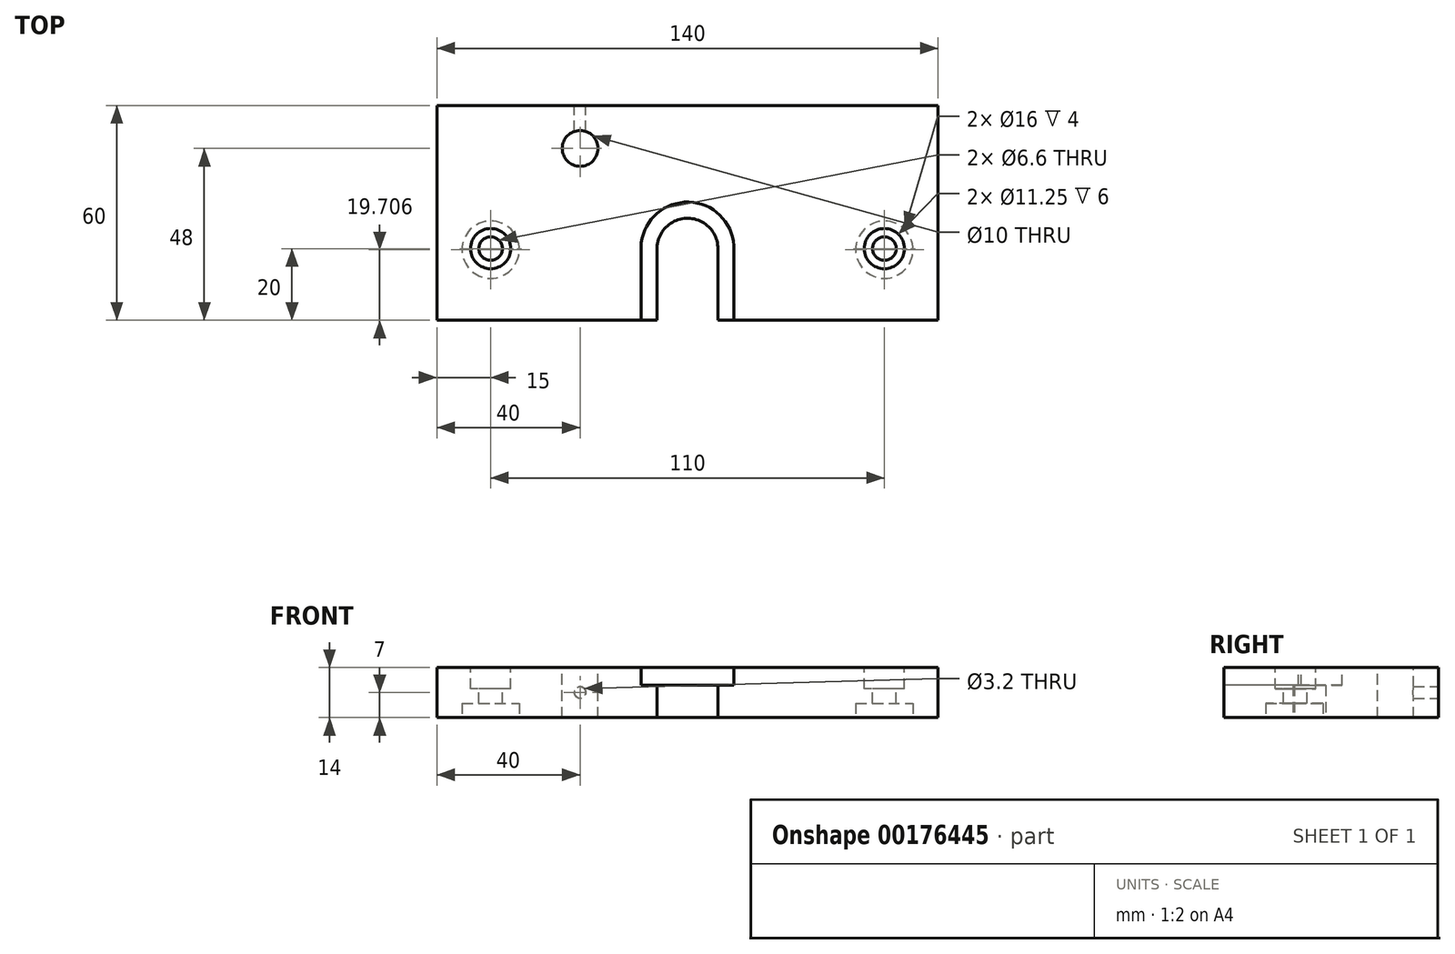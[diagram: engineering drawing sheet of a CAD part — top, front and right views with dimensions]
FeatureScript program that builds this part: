
annotation { "Feature Type Name" : "Feature", "Feature Type Description" : "" }
export const myFeature = defineFeature(function(context is Context, id is Id, definition is map)
    precondition{}
    {
        {
            var Q0;
            Q0=qCreatedBy(makeId("Top.planeOp"),FACE);
            var sketch = newSketch(context, id + "F0", { "sketchPlane" : qUnion([Q0])});
            skLineSegment(sketch, "E0.bottom", {"start": v(70, -30) * mm, "end": v(8.47, -30) * mm});
            skLineSegment(sketch, "E0.top", {"start": v(70, 30) * mm, "end": v(-70, 30) * mm});
            skLineSegment(sketch, "E0.left", {"start": v(70, -30) * mm, "end": v(70, 30) * mm});
            skLineSegment(sketch, "E0.right", {"start": v(-70, -30) * mm, "end": v(-70, 30) * mm});
            skPoint(sketch, "E0.middle", {"position": v(0, 0) * mm});
            skLineSegment(sketch, "E1.trimOffspring", {"start": v(-8.5, -30) * mm, "end": v(-70, -30) * mm});
            skPoint(sketch, "E2.center.orphan", {"position": v(0, -10) * mm});
            skArc(sketch, "E3", {"start": v(8.47, -10.67) * mm, "mid": v(0.19, -1.5) * mm, "end": v(-8.5, -10.3) * mm});
            skLineSegment(sketch, "E4", {"start": v(-8.5, -9.7) * mm, "end": v(-8.5, -30) * mm});
            skLineSegment(sketch, "E5", {"start": v(8.47, -10.67) * mm, "end": v(8.47, -30) * mm});
            skSolve(sketch);
        }
        {
            var Q0;
            Q0=makeQuery(id+"F0.imprint","IMPRINT",FACE,{"disambiguationData":[TD([[makeQuery(id+"F0.imprint","IMPRINT",EDGE,{"derivedFrom":sQuery(id+"F0.wireOp",EDGE,"E0.bottom")}),-1.0]])]});
            extrude(context, id + "F1", {"entities" : qUnion([Q0]), "depth" : 14 * mm});
        }
        {
            var Q0;
            Q0=makeQuery(id+"F1.opExtrude","CAP_FACE",FACE,{"disambiguationData":[OSD([sQuery(id+"F0.wireOp",EDGE,"E0.bottom"),sQuery(id+"F0.wireOp",EDGE,"E0.top"),sQuery(id+"F0.wireOp",EDGE,"E0.left"),sQuery(id+"F0.wireOp",EDGE,"E0.right"),sQuery(id+"F0.wireOp",EDGE,"E1.trimOffspring"),sQuery(id+"F0.wireOp",EDGE,"E3"),sQuery(id+"F0.wireOp",EDGE,"E4"),sQuery(id+"F0.wireOp",EDGE,"E5")])],"isStart":false});
            var sketch = newSketch(context, id + "F2", { "sketchPlane" : qUnion([Q0])});
            skArc(sketch, "E6", {"start": v(12.97, -10.87) * mm, "mid": v(-0.37, 3) * mm, "end": v(-12.9, -11.6) * mm});
            skLineSegment(sketch, "E7", {"start": v(-12.9, -8.4) * mm, "end": v(-12.9, -30) * mm});
            skLineSegment(sketch, "E8", {"start": v(12.97, -9.13) * mm, "end": v(12.97, -30) * mm});
            skSolve(sketch);
        }
        {
            var Q0;
            Q0=makeQuery(id+"F2.imprint","IMPRINT",FACE,{"disambiguationData":[TD([[makeQuery(id+"F2.imprint","IMPRINT",EDGE,{"derivedFrom":makeQuery(id+"F1.opExtrude","CAP_EDGE",EDGE,{"disambiguationData":[OSD([sQuery(id+"F0.wireOp",EDGE,"E3")])],"isStart":false})}),-1.0]])]});
            extrude(context, id + "F3", {"entities" : qUnion([Q0]), "operationType" : NewBodyOperationType.REMOVE, "oppositeDirection" : true, "depth" : 5 * mm});
        }
        {
            var Q0;
            Q0=makeQuery(id+"F1.opExtrude","CAP_FACE",FACE,{"disambiguationData":[OSD([sQuery(id+"F0.wireOp",EDGE,"E0.bottom"),sQuery(id+"F0.wireOp",EDGE,"E0.top"),sQuery(id+"F0.wireOp",EDGE,"E0.left"),sQuery(id+"F0.wireOp",EDGE,"E0.right"),sQuery(id+"F0.wireOp",EDGE,"E1.trimOffspring"),sQuery(id+"F0.wireOp",EDGE,"E3"),sQuery(id+"F0.wireOp",EDGE,"E4"),sQuery(id+"F0.wireOp",EDGE,"E5")])],"isStart":false});
            var sketch = newSketch(context, id + "F4", { "sketchPlane" : qUnion([Q0])});
            skCircle(sketch, "E9", {"center": v(-30, 18) * mm, "radius": 5 * mm});
            skSolve(sketch);
        }
        {
            var Q0;
            Q0=sQuery(id+"F4.wireOp",VERTEX,"E9.center");
            var Q1;
            Q1=makeQuery(id+"F1.opExtrude","SWEPT_BODY",BODY,{"disambiguationData":[OSD([sQuery(id+"F0.wireOp",EDGE,"E0.bottom"),sQuery(id+"F0.wireOp",EDGE,"E0.top"),sQuery(id+"F0.wireOp",EDGE,"E0.left"),sQuery(id+"F0.wireOp",EDGE,"E0.right"),sQuery(id+"F0.wireOp",EDGE,"E1.trimOffspring"),sQuery(id+"F0.wireOp",EDGE,"E3"),sQuery(id+"F0.wireOp",EDGE,"E4"),sQuery(id+"F0.wireOp",EDGE,"E5")])]});
            hole(context, id + "F5", {"style" : HoleStyle.SIMPLE, "endStyle" : HoleEndStyle.THROUGH, "holeDiameter" : 10 * mm, "startFromSketch" : true, "locations" : qUnion([Q0]), "scope" : qUnion([Q1]), "isTappedThrough" : true});
        }
        {
            var Q0;
            Q0=makeQuery(id+"F1.opExtrude","CAP_FACE",FACE,{"disambiguationData":[OSD([sQuery(id+"F0.wireOp",EDGE,"E0.bottom"),sQuery(id+"F0.wireOp",EDGE,"E0.top"),sQuery(id+"F0.wireOp",EDGE,"E0.left"),sQuery(id+"F0.wireOp",EDGE,"E0.right"),sQuery(id+"F0.wireOp",EDGE,"E1.trimOffspring"),sQuery(id+"F0.wireOp",EDGE,"E3"),sQuery(id+"F0.wireOp",EDGE,"E4"),sQuery(id+"F0.wireOp",EDGE,"E5")])],"isStart":true});
            var sketch = newSketch(context, id + "F6", { "sketchPlane" : qUnion([Q0])});
            skCircle(sketch, "E10", {"center": v(-55, 10.3) * mm, "radius": 8 * mm});
            skCircle(sketch, "E11", {"center": v(55, 10.3) * mm, "radius": 8 * mm});
            skSolve(sketch);
        }
        {
            var Q0;
            Q0=makeQuery(id+"F6.imprint","IMPRINT",FACE,{"disambiguationData":[TD([[makeQuery(id+"F6.imprint","IMPRINT",EDGE,{"derivedFrom":sQuery(id+"F6.wireOp",EDGE,"E10")}),1.0]])]});
            var Q1;
            Q1=makeQuery(id+"F6.imprint","IMPRINT",FACE,{"disambiguationData":[TD([[makeQuery(id+"F6.imprint","IMPRINT",EDGE,{"derivedFrom":sQuery(id+"F6.wireOp",EDGE,"E11")}),1.0]])]});
            extrude(context, id + "F7", {"entities" : qUnion([Q0, Q1]), "operationType" : NewBodyOperationType.REMOVE, "oppositeDirection" : true, "depth" : 4 * mm});
        }
        {
            var Q0;
            Q0=makeQuery(id+"F1.opExtrude","CAP_FACE",FACE,{"disambiguationData":[OSD([sQuery(id+"F0.wireOp",EDGE,"E0.bottom"),sQuery(id+"F0.wireOp",EDGE,"E0.top"),sQuery(id+"F0.wireOp",EDGE,"E0.left"),sQuery(id+"F0.wireOp",EDGE,"E0.right"),sQuery(id+"F0.wireOp",EDGE,"E1.trimOffspring"),sQuery(id+"F0.wireOp",EDGE,"E3"),sQuery(id+"F0.wireOp",EDGE,"E4"),sQuery(id+"F0.wireOp",EDGE,"E5")])],"isStart":false});
            var sketch = newSketch(context, id + "F8", { "sketchPlane" : qUnion([Q0])});
            skCircle(sketch, "E12", {"center": v(-55, -10) * mm, "radius": 5 * mm});
            skCircle(sketch, "E13", {"center": v(55, -10) * mm, "radius": 5 * mm});
            skSolve(sketch);
        }
        {
            var Q0;
            Q0=sQuery(id+"F8.wireOp",VERTEX,"E12.center");
            var Q1;
            Q1=sQuery(id+"F8.wireOp",VERTEX,"E13.center");
            var Q2;
            Q2=makeQuery(id+"F1.opExtrude","SWEPT_BODY",BODY,{"disambiguationData":[OSD([sQuery(id+"F0.wireOp",EDGE,"E0.bottom"),sQuery(id+"F0.wireOp",EDGE,"E0.top"),sQuery(id+"F0.wireOp",EDGE,"E0.left"),sQuery(id+"F0.wireOp",EDGE,"E0.right"),sQuery(id+"F0.wireOp",EDGE,"E1.trimOffspring"),sQuery(id+"F0.wireOp",EDGE,"E3"),sQuery(id+"F0.wireOp",EDGE,"E4"),sQuery(id+"F0.wireOp",EDGE,"E5")])]});
            hole(context, id + "F9", {"style" : HoleStyle.C_BORE, "endStyle" : HoleEndStyle.THROUGH, "standardTappedOrClearance" : lookupTablePath({ "standard" : "ISO", "fit" : "Normal", "size" : "M6", "type" : "Clearance" }), "standardBlindInLast" : lookupTablePath({ "fit" : "Standard", "standard" : "ISO", "size" : "M6", "type" : "Clearance" }), "holeDiameter" : 6.6 * mm, "cBoreDiameter" : 11.25 * mm, "cBoreDepth" : 6 * mm, "startFromSketch" : true, "locations" : qUnion([Q0, Q1]), "scope" : qUnion([Q2]), "isTappedThrough" : true});
        }
        {
            var Q0;
            Q0=makeQuery(id+"F1.opExtrude","SWEPT_FACE",FACE,{"disambiguationData":[OSD([sQuery(id+"F0.wireOp",EDGE,"E0.top")])]});
            var sketch = newSketch(context, id + "F10", { "sketchPlane" : qUnion([Q0])});
            skCircle(sketch, "E14", {"center": v(30, 7) * mm, "radius": 2.16 * mm});
            skPoint(sketch, "E14.centerSnap0", {"position": v(70, 7) * mm});
            skSolve(sketch);
        }
        {
            var Q0;
            Q0=sQuery(id+"F10.wireOp",VERTEX,"E14.center");
            var Q1;
            Q1=makeQuery(id+"F1.opExtrude","SWEPT_BODY",BODY,{"disambiguationData":[OSD([sQuery(id+"F0.wireOp",EDGE,"E0.bottom"),sQuery(id+"F0.wireOp",EDGE,"E0.top"),sQuery(id+"F0.wireOp",EDGE,"E0.left"),sQuery(id+"F0.wireOp",EDGE,"E0.right"),sQuery(id+"F0.wireOp",EDGE,"E1.trimOffspring"),sQuery(id+"F0.wireOp",EDGE,"E3"),sQuery(id+"F0.wireOp",EDGE,"E4"),sQuery(id+"F0.wireOp",EDGE,"E5")])]});
            hole(context, id + "F11", {"style" : HoleStyle.SIMPLE, "endStyle" : HoleEndStyle.BLIND, "standardTappedOrClearance" : lookupTablePath({ "standard" : "ISO", "engagement" : "75%", "pitch" : "0.75 mm", "size" : "M4", "type" : "Tapped" }), "standardBlindInLast" : lookupTablePath({ "standard" : "ISO", "engagement" : "75%", "pitch" : "0.75 mm", "size" : "M4", "type" : "Tapped" }), "holeDiameter" : 3.2 * mm, "holeDepth" : 9 * mm, "startFromSketch" : true, "locations" : qUnion([Q0]), "scope" : qUnion([Q1])});
        }
    });
